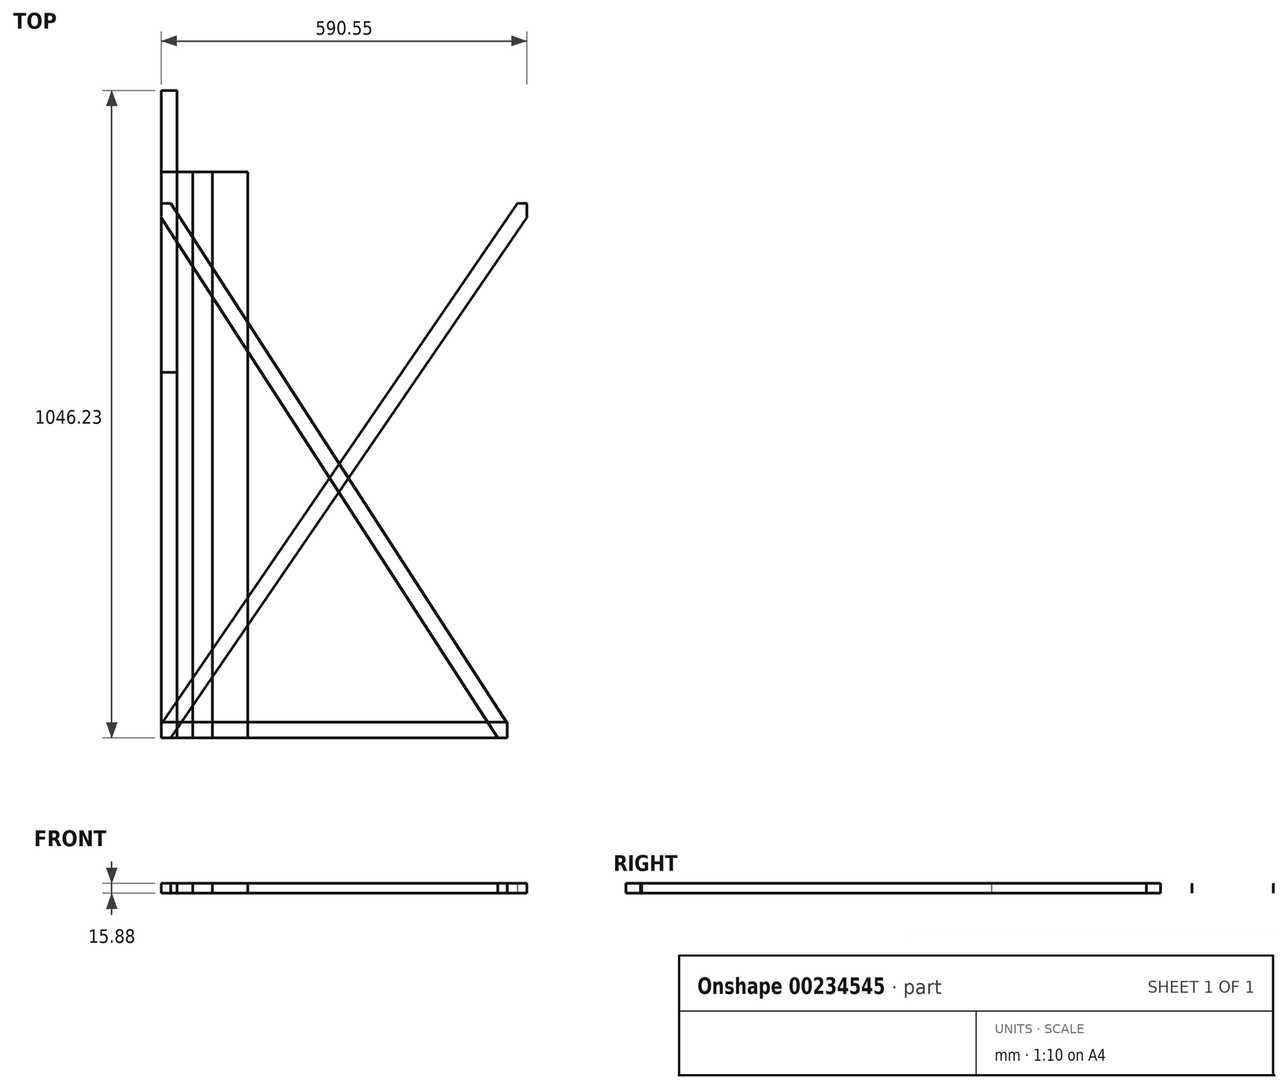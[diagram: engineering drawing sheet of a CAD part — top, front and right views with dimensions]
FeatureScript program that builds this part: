
annotation { "Feature Type Name" : "Feature", "Feature Type Description" : "" }
export const myFeature = defineFeature(function(context is Context, id is Id, definition is map)
    precondition{}
    {
        {
            var Q0;
            Q0=qCreatedBy(makeId("Top.planeOp"),FACE);
            var sketch = newSketch(context, id + "F0", { "sketchPlane" : qUnion([Q0])});
            skLineSegment(sketch, "E0.bottom", {"start": v(0, 0) * mm, "end": v(139.7, 0) * mm});
            skLineSegment(sketch, "E0.top", {"start": v(0, 914.4) * mm, "end": v(139.7, 914.4) * mm});
            skLineSegment(sketch, "E0.left", {"start": v(0, 0) * mm, "end": v(0, 914.4) * mm});
            skLineSegment(sketch, "E0.right", {"start": v(139.7, 0) * mm, "end": v(139.7, 914.4) * mm});
            skSolve(sketch);
        }
        {
            var Q0;
            Q0 = qSketchRegion(id + "F0", true);
            extrude(context, id + "F1", {"entities" : qUnion([Q0]), "depth" : 15.88 * mm});
        }
        {
            var Q0;
            Q0=qCreatedBy(makeId("Top.planeOp"),FACE);
            var sketch = newSketch(context, id + "F2", { "sketchPlane" : qUnion([Q0])});
            skLineSegment(sketch, "E1.bottom", {"start": v(0, 0) * mm, "end": v(82.55, 0) * mm});
            skLineSegment(sketch, "E1.top", {"start": v(0, 914.4) * mm, "end": v(82.55, 914.4) * mm});
            skLineSegment(sketch, "E1.left", {"start": v(0, 0) * mm, "end": v(0, 914.4) * mm});
            skLineSegment(sketch, "E1.right", {"start": v(82.55, 0) * mm, "end": v(82.55, 914.4) * mm});
            skSolve(sketch);
        }
        {
            var Q0;
            Q0 = qSketchRegion(id + "F2", true);
            extrude(context, id + "F3", {"entities" : qUnion([Q0]), "depth" : 15.88 * mm});
        }
        {
            var Q0;
            Q0=qCreatedBy(makeId("Top.planeOp"),FACE);
            var sketch = newSketch(context, id + "F4", { "sketchPlane" : qUnion([Q0])});
            skLineSegment(sketch, "E2.bottom", {"start": v(0, 0) * mm, "end": v(50.8, 0) * mm});
            skLineSegment(sketch, "E2.top", {"start": v(0, 914.4) * mm, "end": v(50.8, 914.4) * mm});
            skLineSegment(sketch, "E2.left", {"start": v(0, 0) * mm, "end": v(0, 914.4) * mm});
            skLineSegment(sketch, "E2.right", {"start": v(50.8, 0) * mm, "end": v(50.8, 914.4) * mm});
            skSolve(sketch);
        }
        {
            var Q0;
            Q0 = qSketchRegion(id + "F4", true);
            extrude(context, id + "F5", {"entities" : qUnion([Q0]), "depth" : 15.88 * mm});
        }
        {
            var Q0;
            Q0=qCreatedBy(makeId("Top.planeOp"),FACE);
            var sketch = newSketch(context, id + "F6", { "sketchPlane" : qUnion([Q0])});
            skLineSegment(sketch, "E3.bottom", {"start": v(0, 0) * mm, "end": v(25.4, 0) * mm});
            skLineSegment(sketch, "E3.top", {"start": v(0, 914.4) * mm, "end": v(25.4, 914.4) * mm});
            skLineSegment(sketch, "E3.left", {"start": v(0, 0) * mm, "end": v(0, 914.4) * mm});
            skLineSegment(sketch, "E3.right", {"start": v(25.4, 0) * mm, "end": v(25.4, 914.4) * mm});
            skSolve(sketch);
        }
        {
            var Q0;
            Q0 = qSketchRegion(id + "F6", true);
            extrude(context, id + "F7", {"entities" : qUnion([Q0]), "depth" : 15.88 * mm});
        }
        {
            var Q0;
            Q0=qCreatedBy(makeId("Top.planeOp"),FACE);
            var sketch = newSketch(context, id + "F8", { "sketchPlane" : qUnion([Q0])});
            skLineSegment(sketch, "E4.bottom", {"start": v(0, 0) * mm, "end": v(25.4, 0) * mm});
            skLineSegment(sketch, "E4.top", {"start": v(0, 590.55) * mm, "end": v(25.4, 590.55) * mm});
            skLineSegment(sketch, "E4.left", {"start": v(0, 0) * mm, "end": v(0, 590.55) * mm});
            skLineSegment(sketch, "E4.right", {"start": v(25.4, 0) * mm, "end": v(25.4, 590.55) * mm});
            skSolve(sketch);
        }
        {
            var Q0;
            Q0 = qSketchRegion(id + "F8", true);
            extrude(context, id + "F9", {"entities" : qUnion([Q0]), "depth" : 15.88 * mm});
        }
        {
            var Q0;
            Q0=qCreatedBy(makeId("Top.planeOp"),FACE);
            var sketch = newSketch(context, id + "F10", { "sketchPlane" : qUnion([Q0])});
            skLineSegment(sketch, "E5.bottom", {"start": v(0, 0) * mm, "end": v(25.4, 0) * mm});
            skLineSegment(sketch, "E5.top", {"start": v(0, 1046.23) * mm, "end": v(25.4, 1046.23) * mm});
            skLineSegment(sketch, "E5.left", {"start": v(0, 0) * mm, "end": v(0, 1046.23) * mm});
            skLineSegment(sketch, "E5.right", {"start": v(25.4, 0) * mm, "end": v(25.4, 1046.23) * mm});
            skSolve(sketch);
        }
        {
            var Q0;
            Q0 = qSketchRegion(id + "F10", true);
            extrude(context, id + "F11", {"entities" : qUnion([Q0]), "depth" : 15.88 * mm});
        }
        {
            var Q0;
            Q0=qCreatedBy(makeId("Top.planeOp"),FACE);
            var sketch = newSketch(context, id + "F12", { "sketchPlane" : qUnion([Q0])});
            skLineSegment(sketch, "E6.bottom", {"start": v(0, 0) * mm, "end": v(590.55, 0) * mm, "construction": true});
            skLineSegment(sketch, "E6.top", {"start": v(0, 863.6) * mm, "end": v(590.55, 863.6) * mm, "construction": true});
            skLineSegment(sketch, "E6.left", {"start": v(0, 0) * mm, "end": v(0, 863.6) * mm, "construction": true});
            skLineSegment(sketch, "E6.right", {"start": v(590.55, 0) * mm, "end": v(590.55, 863.6) * mm, "construction": true});
            skLineSegment(sketch, "E7", {"start": v(0, 0) * mm, "end": v(590.55, 863.6) * mm, "construction": true});
            skLineSegment(sketch, "E8.left", {"start": v(0, 22.5) * mm, "end": v(575.16, 863.6) * mm});
            skLineSegment(sketch, "E8.right", {"start": v(15.39, 0) * mm, "end": v(590.55, 841.1) * mm});
            skLineSegment(sketch, "E9", {"start": v(0, 0) * mm, "end": v(0, 22.5) * mm});
            skLineSegment(sketch, "E10", {"start": v(0, 0) * mm, "end": v(15.39, 0) * mm});
            skLineSegment(sketch, "E11", {"start": v(575.16, 863.6) * mm, "end": v(590.55, 863.6) * mm});
            skLineSegment(sketch, "E12", {"start": v(590.55, 863.6) * mm, "end": v(590.55, 841.1) * mm});
            skSolve(sketch);
        }
        {
            var Q0;
            Q0 = qSketchRegion(id + "F12", true);
            extrude(context, id + "F13", {"entities" : qUnion([Q0]), "depth" : 15.88 * mm});
        }
        {
            var Q0;
            Q0=qCreatedBy(makeId("Top.planeOp"),FACE);
            var sketch = newSketch(context, id + "F14", { "sketchPlane" : qUnion([Q0])});
            skLineSegment(sketch, "E13.bottom", {"start": v(0, 0) * mm, "end": v(558.8, 0) * mm});
            skLineSegment(sketch, "E13.top", {"start": v(0, 25.4) * mm, "end": v(558.8, 25.4) * mm});
            skLineSegment(sketch, "E13.left", {"start": v(0, 0) * mm, "end": v(0, 25.4) * mm});
            skLineSegment(sketch, "E13.right", {"start": v(558.8, 0) * mm, "end": v(558.8, 25.4) * mm});
            skSolve(sketch);
        }
        {
            var Q0;
            Q0 = qSketchRegion(id + "F14", true);
            extrude(context, id + "F15", {"entities" : qUnion([Q0]), "depth" : 15.88 * mm});
        }
        {
            var Q0;
            Q0=qCreatedBy(makeId("Top.planeOp"),FACE);
            var sketch = newSketch(context, id + "F16", { "sketchPlane" : qUnion([Q0])});
            skLineSegment(sketch, "E14", {"start": v(0, 863.6) * mm, "end": v(558.8, 863.6) * mm, "construction": true});
            skLineSegment(sketch, "E15", {"start": v(558.8, 863.6) * mm, "end": v(558.8, 0) * mm, "construction": true});
            skLineSegment(sketch, "E16", {"start": v(0, 863.6) * mm, "end": v(0, 0) * mm, "construction": true});
            skLineSegment(sketch, "E17", {"start": v(0, 0) * mm, "end": v(558.8, 0) * mm, "construction": true});
            skLineSegment(sketch, "E18", {"start": v(0, 863.6) * mm, "end": v(558.8, 0) * mm, "construction": true});
            skLineSegment(sketch, "E19", {"start": v(0, 840.22) * mm, "end": v(543.67, 0) * mm});
            skLineSegment(sketch, "E20", {"start": v(15.13, 863.6) * mm, "end": v(558.8, 23.38) * mm});
            skLineSegment(sketch, "E21", {"start": v(0, 840.22) * mm, "end": v(0, 863.6) * mm});
            skLineSegment(sketch, "E22", {"start": v(0, 863.6) * mm, "end": v(15.13, 863.6) * mm});
            skLineSegment(sketch, "E23", {"start": v(558.8, 0) * mm, "end": v(558.8, 23.38) * mm});
            skLineSegment(sketch, "E24", {"start": v(543.67, 0) * mm, "end": v(558.8, 0) * mm});
            skSolve(sketch);
        }
        {
            var Q0;
            Q0 = qSketchRegion(id + "F16", true);
            extrude(context, id + "F17", {"entities" : qUnion([Q0]), "depth" : 15.88 * mm});
        }
    });
